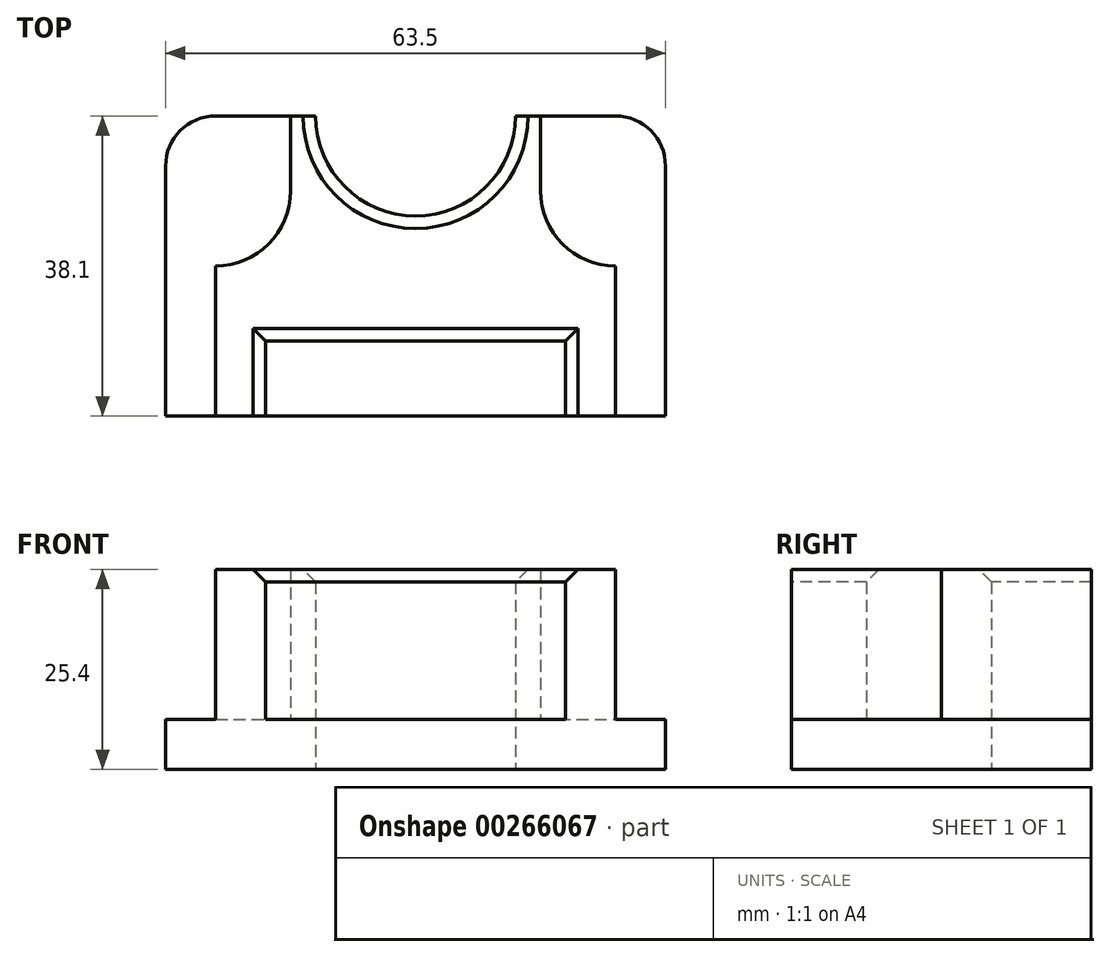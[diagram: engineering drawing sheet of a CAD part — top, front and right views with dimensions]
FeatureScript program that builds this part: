
annotation { "Feature Type Name" : "Feature", "Feature Type Description" : "" }
export const myFeature = defineFeature(function(context is Context, id is Id, definition is map)
    precondition{}
    {
        {
            var Q0;
            Q0=qCreatedBy(makeId("Top.planeOp"),FACE);
            var sketch = newSketch(context, id + "F0", { "sketchPlane" : qUnion([Q0])});
            skLineSegment(sketch, "E0.bottom", {"start": v(0, 0) * mm, "end": v(63.5, 0) * mm});
            skLineSegment(sketch, "E0.top", {"start": v(0, -38.1) * mm, "end": v(63.5, -38.1) * mm});
            skLineSegment(sketch, "E0.left", {"start": v(0, 0) * mm, "end": v(0, -38.1) * mm});
            skLineSegment(sketch, "E0.right", {"start": v(63.5, 0) * mm, "end": v(63.5, -38.1) * mm});
            skSolve(sketch);
        }
        {
            var Q0;
            Q0 = qSketchRegion(id + "F0", true);
            extrude(context, id + "F1", {"entities" : qUnion([Q0]), "depth" : 6.35 * mm});
        }
        {
            var Q0;
            Q0=makeQuery(id+"F1.opExtrude","CAP_FACE",FACE,{"disambiguationData":[OSD([sQuery(id+"F0.wireOp",EDGE,"E0.bottom"),sQuery(id+"F0.wireOp",EDGE,"E0.top"),sQuery(id+"F0.wireOp",EDGE,"E0.left"),sQuery(id+"F0.wireOp",EDGE,"E0.right")])],"isStart":false});
            var sketch = newSketch(context, id + "F2", { "sketchPlane" : qUnion([Q0])});
            skLineSegment(sketch, "E1", {"start": v(6.35, -38.1) * mm, "end": v(6.35, -19.05) * mm});
            skLineSegment(sketch, "E2", {"start": v(57.15, -38.1) * mm, "end": v(57.15, -19.05) * mm});
            skLineSegment(sketch, "E3", {"start": v(6.35, -38.1) * mm, "end": v(12.7, -38.1) * mm});
            skLineSegment(sketch, "E4", {"start": v(57.15, -38.1) * mm, "end": v(50.8, -38.1) * mm});
            skLineSegment(sketch, "E5", {"start": v(12.7, -38.1) * mm, "end": v(12.7, -28.58) * mm});
            skLineSegment(sketch, "E6", {"start": v(50.8, -38.1) * mm, "end": v(50.8, -28.58) * mm});
            skLineSegment(sketch, "E7", {"start": v(50.8, -28.58) * mm, "end": v(12.7, -28.58) * mm});
            skLineSegment(sketch, "E8", {"start": v(15.87, 0) * mm, "end": v(19.05, 0) * mm});
            skArc(sketch, "E9", {"start": v(6.35, -19.05) * mm, "mid": v(13.09, -16.26) * mm, "end": v(15.88, -9.53) * mm});
            skLineSegment(sketch, "E10", {"start": v(15.88, -9.53) * mm, "end": v(15.87, 0) * mm});
            skArc(sketch, "E11", {"start": v(57.15, -19.05) * mm, "mid": v(50.41, -16.26) * mm, "end": v(47.62, -9.53) * mm});
            skLineSegment(sketch, "E12", {"start": v(47.62, -9.53) * mm, "end": v(47.62, 0) * mm});
            skLineSegment(sketch, "E13", {"start": v(47.62, 0) * mm, "end": v(44.45, 0) * mm});
            skArc(sketch, "E14", {"start": v(44.45, 0) * mm, "mid": v(31.75, -12.7) * mm, "end": v(19.05, 0) * mm});
            skSolve(sketch);
        }
        {
            var Q0;
            Q0 = qSketchRegion(id + "F2", true);
            extrude(context, id + "F3", {"entities" : qUnion([Q0]), "operationType" : NewBodyOperationType.ADD, "depth" : 19.05 * mm});
        }
        {
            var Q0;
            {var subQ0=sQuery(id+"F0.wireOp",EDGE,"E0.bottom");Q0=makeQuery(id+"F3.boolean.opBoolean","SPLIT",FACE,{"disambiguationData":[TD([makeQuery(id+"F3.opExtrude","SWEPT_FACE",FACE,{"disambiguationData":[OSD([sQuery(id+"F2.wireOp",EDGE,"E14")])]})])],"derivedFrom":makeQuery(id+"F1.opExtrude","CAP_FACE",FACE,{"disambiguationData":[OSD([subQ0,sQuery(id+"F0.wireOp",EDGE,"E0.top"),sQuery(id+"F0.wireOp",EDGE,"E0.left"),sQuery(id+"F0.wireOp",EDGE,"E0.right")])],"isStart":false})});}
            extrude(context, id + "F4", {"entities" : qUnion([Q0]), "operationType" : NewBodyOperationType.REMOVE, "oppositeDirection" : true, "depth" : 25.4 * mm});
        }
        {
            var Q0;
            Q0=makeQuery(id+"F3.opExtrude","CAP_EDGE",EDGE,{"disambiguationData":[OSD([sQuery(id+"F2.wireOp",EDGE,"E5")])],"isStart":false});
            var Q1;
            Q1=makeQuery(id+"F3.opExtrude","CAP_EDGE",EDGE,{"disambiguationData":[OSD([sQuery(id+"F2.wireOp",EDGE,"E7")])],"isStart":false});
            var Q2;
            Q2=makeQuery(id+"F3.opExtrude","CAP_EDGE",EDGE,{"disambiguationData":[OSD([sQuery(id+"F2.wireOp",EDGE,"E6")])],"isStart":false});
            var Q3;
            Q3=makeQuery(id+"F3.opExtrude","CAP_EDGE",EDGE,{"disambiguationData":[OSD([sQuery(id+"F2.wireOp",EDGE,"E14")])],"isStart":false});
            chamfer(context, id + "F5", {"entities" : qUnion([Q0, Q1, Q2, Q3]), "width" : 1.59 * mm, "tangentPropagation" : true});
        }
        {
            var Q0;
            {var subQ0=sQuery(id+"F0.wireOp",EDGE,"E0.left");var subQ1=sQuery(id+"F0.wireOp",EDGE,"E0.top");var subQ2=sQuery(id+"F0.wireOp",EDGE,"E0.bottom");Q0=makeQuery(id+"F3.boolean.opBoolean","SPLIT",FACE,{"disambiguationData":[TD([makeQuery(id+"F1.opExtrude","SWEPT_FACE",FACE,{"disambiguationData":[OSD([subQ0])]})])],"derivedFrom":makeQuery(id+"F1.opExtrude","CAP_FACE",FACE,{"disambiguationData":[OSD([subQ2,subQ1,subQ0,sQuery(id+"F0.wireOp",EDGE,"E0.right")])],"isStart":false})});}
            var sketch = newSketch(context, id + "F6", { "sketchPlane" : qUnion([Q0])});
            skLineSegment(sketch, "E15", {"start": v(0, 0) * mm, "end": v(6.35, 0) * mm});
            skArc(sketch, "E16", {"start": v(0, -6.35) * mm, "mid": v(1.86, -1.86) * mm, "end": v(6.35, 0) * mm});
            skLineSegment(sketch, "E17", {"start": v(0, -6.35) * mm, "end": v(0, 0) * mm});
            skSolve(sketch);
        }
        {
            var Q0;
            Q0 = qSketchRegion(id + "F6", true);
            extrude(context, id + "F7", {"entities" : qUnion([Q0]), "operationType" : NewBodyOperationType.REMOVE, "oppositeDirection" : true, "depth" : 25.4 * mm});
        }
        {
            var Q0;
            {var subQ0=sQuery(id+"F0.wireOp",EDGE,"E0.right");var subQ1=sQuery(id+"F0.wireOp",EDGE,"E0.top");var subQ2=sQuery(id+"F0.wireOp",EDGE,"E0.bottom");Q0=makeQuery(id+"F3.boolean.opBoolean","SPLIT",FACE,{"disambiguationData":[TD([makeQuery(id+"F1.opExtrude","SWEPT_FACE",FACE,{"disambiguationData":[OSD([subQ0])]})])],"derivedFrom":makeQuery(id+"F1.opExtrude","CAP_FACE",FACE,{"disambiguationData":[OSD([subQ2,subQ1,sQuery(id+"F0.wireOp",EDGE,"E0.left"),subQ0])],"isStart":false})});}
            var sketch = newSketch(context, id + "F8", { "sketchPlane" : qUnion([Q0])});
            skLineSegment(sketch, "E18", {"start": v(63.5, 0) * mm, "end": v(57.15, 0) * mm});
            skLineSegment(sketch, "E19", {"start": v(63.5, -6.35) * mm, "end": v(63.5, 0) * mm});
            skArc(sketch, "E20", {"start": v(63.5, -6.35) * mm, "mid": v(61.64, -1.86) * mm, "end": v(57.15, 0) * mm});
            skSolve(sketch);
        }
        {
            var Q0;
            Q0 = qSketchRegion(id + "F8", true);
            extrude(context, id + "F9", {"entities" : qUnion([Q0]), "operationType" : NewBodyOperationType.REMOVE, "oppositeDirection" : true, "depth" : 25.4 * mm});
        }
    });
